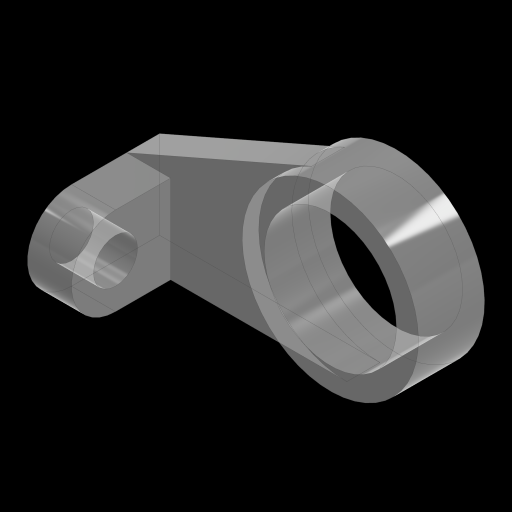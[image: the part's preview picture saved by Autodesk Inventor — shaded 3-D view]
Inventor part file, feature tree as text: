
AUTODESK INVENTOR PART (.ipt)
format: ipt  version: 2024 (Build 280153000, 153)  size: 166,912 bytes
history: native  units: in
note: dims shown in document units (in); Inventor stores cm internally (conversion verified against a paired STEP export)
features: sketch x6, extrude x4, hole x2
ambient origin geometry x8: Origin, YZ Plane, XZ Plane, XY Plane, X Axis, Y Axis, Z Axis, Center Point
bodies: Solid1 (feature_tree)
feature tree (12):
  extrude  "Extrusion1"  Depth=5.0in
  extrude  "Extrusion2"  Depth=0.75in TaperAngle=0.0deg
  extrude  "Extrusion3"  Depth=1.5in TaperAngle=0.0deg
  extrude  "Extrusion4"  Depth=2.0in
  hole  "Hole1"  [1 undecoded]
  hole  "Hole2"  [1 undecoded]
  sketch  "Sketch1"  dims[d0=5.0in d1=4.0in]
  sketch  "Sketch2"  dims[d2=2.0in d3=0.75in d4=0.0in]
  sketch  "Sketch3"  dims[d5=4.0in d6=1.5in d7=0.0in]
  sketch  "Sketch4"  dims[d8=1.0in d9=2.0in]
  sketch  "Sketch5"  dims[d10=1.25in d11=0.0in d12=1.0in d13=0.0in]
  sketch  "Sketch6"  dims[d14=1.0in d15=0.75in d16=0.375in d17=0.25in d18=0.5635in d19=1.0in d20=0.8108in d21=3.0in d22=0.75in d23=0.375in d24=0.25in d25=0.5635in d26=1.0in d27=0.8108in]
note: 2 required parameter values undecoded (feature->parameter linkage not recoverable at this tier; creation-order binding heuristic only, values carry confidence <= 0.55)
